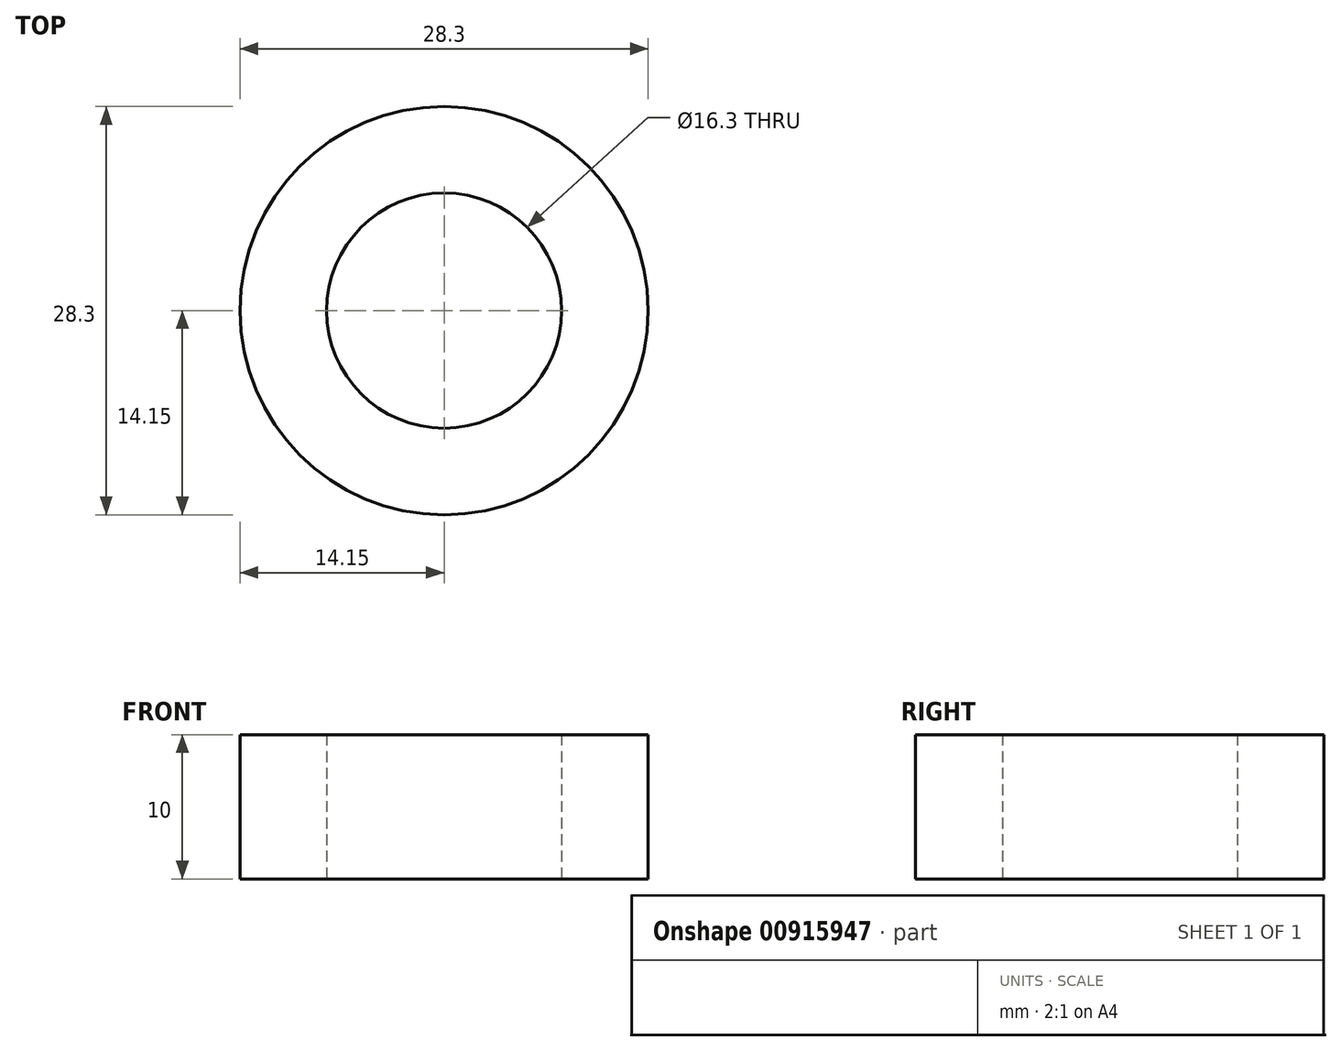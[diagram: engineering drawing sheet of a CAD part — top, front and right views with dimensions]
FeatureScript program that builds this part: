
annotation { "Feature Type Name" : "Feature", "Feature Type Description" : "" }
export const myFeature = defineFeature(function(context is Context, id is Id, definition is map)
    precondition{}
    {
        {
            var Q0;
            Q0=qCreatedBy(makeId("Top.planeOp"),FACE);
            var sketch = newSketch(context, id + "F0", { "sketchPlane" : qUnion([Q0])});
            skCircle(sketch, "E0", {"center": v(0, 0) * mm, "radius": 8.15 * mm});
            skCircle(sketch, "E1", {"center": v(0, 0) * mm, "radius": 14.15 * mm});
            skSolve(sketch);
        }
        {
            var Q0;
            Q0=makeQuery(id+"F0.imprint","IMPRINT",FACE,{"disambiguationData":[TD([[makeQuery(id+"F0.imprint","IMPRINT",EDGE,{"derivedFrom":sQuery(id+"F0.wireOp",EDGE,"E0")}),-1.0]])]});
            extrude(context, id + "F1", {"entities" : qUnion([Q0]), "depth" : 10 * mm, "offsetDistance" : 25 * mm});
        }
    });
